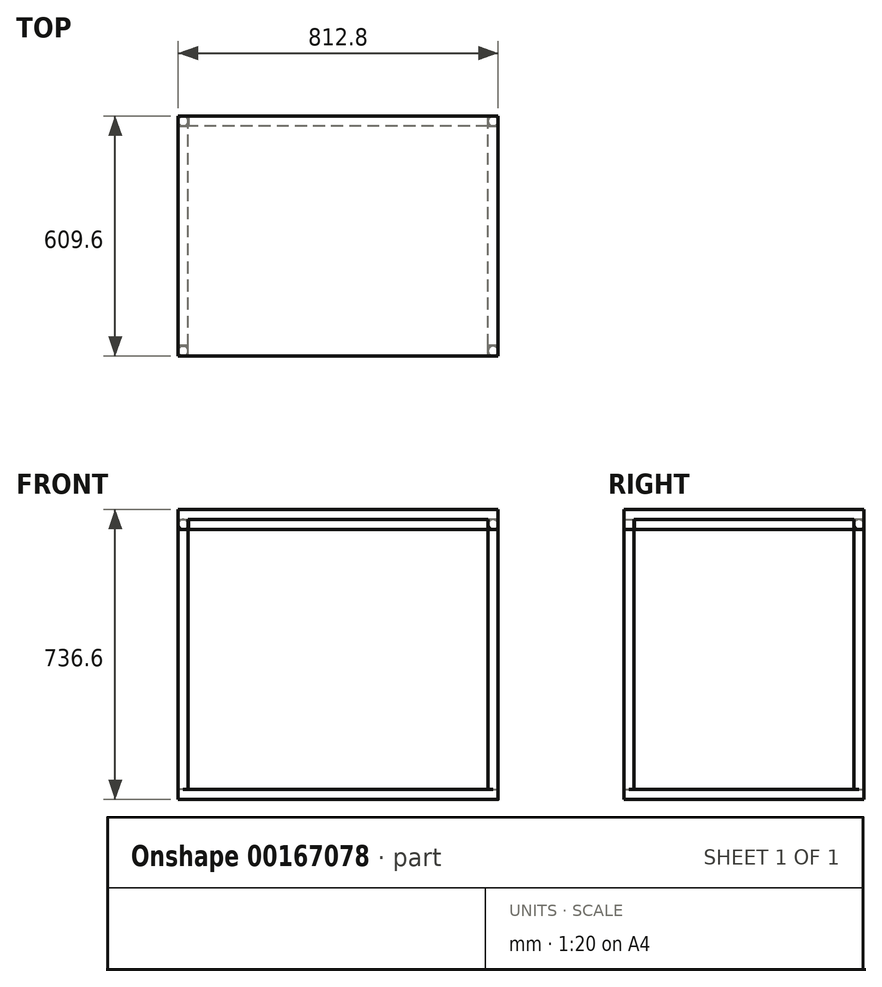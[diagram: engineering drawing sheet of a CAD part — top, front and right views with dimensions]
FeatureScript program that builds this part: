
annotation { "Feature Type Name" : "Feature", "Feature Type Description" : "" }
export const myFeature = defineFeature(function(context is Context, id is Id, definition is map)
    precondition{}
    {
        {
            var Q0;
            Q0=qCreatedBy(makeId("Top.planeOp"),FACE);
            var sketch = newSketch(context, id + "F0", { "sketchPlane" : qUnion([Q0])});
            skLineSegment(sketch, "E0.bottom", {"start": v(406.4, 304.8) * mm, "end": v(-406.4, 304.8) * mm});
            skLineSegment(sketch, "E0.top", {"start": v(406.4, -304.8) * mm, "end": v(-406.4, -304.8) * mm});
            skLineSegment(sketch, "E0.left", {"start": v(406.4, 304.8) * mm, "end": v(406.4, -304.8) * mm});
            skLineSegment(sketch, "E0.right", {"start": v(-406.4, 304.8) * mm, "end": v(-406.4, -304.8) * mm});
            skPoint(sketch, "E0.middle", {"position": v(0, 0) * mm});
            skSolve(sketch);
        }
        {
            var Q0;
            Q0=makeQuery(id+"F0.imprint","IMPRINT",FACE,{"disambiguationData":[TD([[makeQuery(id+"F0.imprint","IMPRINT",EDGE,{"derivedFrom":sQuery(id+"F0.wireOp",EDGE,"E0.bottom")}),1.0]])]});
            extrude(context, id + "F1", {"entities" : qUnion([Q0]), "depth" : 25.4 * mm});
        }
        {
            var Q0;
            Q0=qCreatedBy(makeId("Right.planeOp"),FACE);
            var sketch = newSketch(context, id + "F2", { "sketchPlane" : qUnion([Q0])});
            skLineSegment(sketch, "E1", {"start": v(0, 0) * mm, "end": v(-292.1, 0) * mm});
            skLineSegment(sketch, "E2", {"start": v(0, 0) * mm, "end": v(292.1, 0) * mm});
            skCircle(sketch, "E3", {"center": v(292.1, -12.7) * mm, "radius": 12.7 * mm});
            skSolve(sketch);
        }
        {
            var Q0;
            Q0=qCreatedBy(makeId("Front.planeOp"),FACE);
            var sketch = newSketch(context, id + "F3", { "sketchPlane" : qUnion([Q0])});
            skLineSegment(sketch, "E4", {"start": v(0, 0) * mm, "end": v(-393.7, 0) * mm});
            skLineSegment(sketch, "E5", {"start": v(0, 0) * mm, "end": v(393.7, 0) * mm});
            skCircle(sketch, "E6", {"center": v(-393.7, -12.7) * mm, "radius": 12.7 * mm});
            skCircle(sketch, "E7", {"center": v(393.7, -12.7) * mm, "radius": 12.7 * mm});
            skSolve(sketch);
        }
        {
            var Q0;
            Q0=makeQuery(id+"F1.opExtrude","CAP_FACE",FACE,{"disambiguationData":[OSD([sQuery(id+"F0.wireOp",EDGE,"E0.bottom"),sQuery(id+"F0.wireOp",EDGE,"E0.top"),sQuery(id+"F0.wireOp",EDGE,"E0.left"),sQuery(id+"F0.wireOp",EDGE,"E0.right")])],"isStart":true});
            var sketch = newSketch(context, id + "F4", { "sketchPlane" : qUnion([Q0])});
            skPoint(sketch, "E8.middle", {"position": v(-406.4, -304.8) * mm});
            skLineSegment(sketch, "E9.bottom", {"start": v(-406.4, -304.8) * mm, "end": v(-381, -304.8) * mm});
            skLineSegment(sketch, "E9.top", {"start": v(-406.4, -279.4) * mm, "end": v(-381, -279.4) * mm});
            skLineSegment(sketch, "E9.left", {"start": v(-406.4, -304.8) * mm, "end": v(-406.4, -279.4) * mm});
            skLineSegment(sketch, "E9.right", {"start": v(-381, -304.8) * mm, "end": v(-381, -279.4) * mm});
            skLineSegment(sketch, "E10.bottom", {"start": v(406.4, -304.8) * mm, "end": v(381, -304.8) * mm});
            skLineSegment(sketch, "E10.top", {"start": v(406.4, -279.4) * mm, "end": v(381, -279.4) * mm});
            skLineSegment(sketch, "E10.left", {"start": v(406.4, -304.8) * mm, "end": v(406.4, -279.4) * mm});
            skLineSegment(sketch, "E10.right", {"start": v(381, -304.8) * mm, "end": v(381, -279.4) * mm});
            skLineSegment(sketch, "E11.bottom", {"start": v(406.4, 304.8) * mm, "end": v(381, 304.8) * mm});
            skLineSegment(sketch, "E11.top", {"start": v(406.4, 279.4) * mm, "end": v(381, 279.4) * mm});
            skLineSegment(sketch, "E11.left", {"start": v(406.4, 304.8) * mm, "end": v(406.4, 279.4) * mm});
            skLineSegment(sketch, "E11.right", {"start": v(381, 304.8) * mm, "end": v(381, 279.4) * mm});
            skLineSegment(sketch, "E12.bottom", {"start": v(-406.4, 304.8) * mm, "end": v(-381, 304.8) * mm});
            skLineSegment(sketch, "E12.top", {"start": v(-406.4, 279.4) * mm, "end": v(-381, 279.4) * mm});
            skLineSegment(sketch, "E12.left", {"start": v(-406.4, 304.8) * mm, "end": v(-406.4, 279.4) * mm});
            skLineSegment(sketch, "E12.right", {"start": v(-381, 304.8) * mm, "end": v(-381, 279.4) * mm});
            skSolve(sketch);
        }
        {
            var Q0;
            Q0 = qSketchRegion(id + "F4", true);
            extrude(context, id + "F5", {"entities" : qUnion([Q0]), "operationType" : NewBodyOperationType.ADD, "depth" : 25.4 * mm});
        }
        {
            var Q0;
            Q0=qCreatedBy(makeId("Top.planeOp"),FACE);
            cPlane(context, id + "F6", {"entities" : qUnion([Q0]), "cplaneType" : CPlaneType.OFFSET, "offset" : 25.4 * mm, "oppositeDirection" : true, "width" : 152.4 * mm, "height" : 152.4 * mm});
        }
        {
            var Q0;
            Q0=qCreatedBy(id+"F6.planeOp",FACE);
            var sketch = newSketch(context, id + "F7", { "sketchPlane" : qUnion([Q0])});
            skLineSegment(sketch, "E13", {"start": v(0, 0) * mm, "end": v(-393.7, 0) * mm});
            skLineSegment(sketch, "E14", {"start": v(-393.7, 0) * mm, "end": v(-393.7, -292.1) * mm});
            skLineSegment(sketch, "E15", {"start": v(0, 0) * mm, "end": v(393.7, 0) * mm});
            skLineSegment(sketch, "E16", {"start": v(393.7, 0) * mm, "end": v(393.7, 292.1) * mm});
            skCircle(sketch, "E17", {"center": v(-393.7, -292.1) * mm, "radius": 12.7 * mm});
            skCircle(sketch, "E18", {"center": v(-393.7, 292.1) * mm, "radius": 12.7 * mm});
            skCircle(sketch, "E19", {"center": v(393.7, 292.1) * mm, "radius": 12.7 * mm});
            skCircle(sketch, "E20", {"center": v(393.7, -292.1) * mm, "radius": 12.7 * mm});
            skSolve(sketch);
        }
        {
            var Q0;
            Q0 = qSketchRegion(id + "F7", true);
            extrude(context, id + "F8", {"entities" : qUnion([Q0]), "operationType" : NewBodyOperationType.ADD, "oppositeDirection" : true, "depth" : 685.8 * mm});
        }
        {
            var Q0;
            Q0=qCreatedBy(makeId("Top.planeOp"),FACE);
            cPlane(context, id + "F9", {"entities" : qUnion([Q0]), "cplaneType" : CPlaneType.OFFSET, "offset" : 711.2 * mm, "oppositeDirection" : true, "width" : 152.4 * mm, "height" : 152.4 * mm});
        }
        {
            var Q0;
            Q0=qCreatedBy(id+"F9.planeOp",FACE);
            var sketch = newSketch(context, id + "F10", { "sketchPlane" : qUnion([Q0])});
            skLineSegment(sketch, "E21.bottom", {"start": v(406.4, -304.8) * mm, "end": v(-406.4, -304.8) * mm});
            skLineSegment(sketch, "E21.top", {"start": v(406.4, 304.8) * mm, "end": v(-406.4, 304.8) * mm});
            skLineSegment(sketch, "E21.left", {"start": v(406.4, -304.8) * mm, "end": v(406.4, 304.8) * mm});
            skLineSegment(sketch, "E21.right", {"start": v(-406.4, -304.8) * mm, "end": v(-406.4, 304.8) * mm});
            skPoint(sketch, "E21.middle", {"position": v(0, 0) * mm});
            skSolve(sketch);
        }
        {
            var Q0;
            Q0=makeQuery(id+"F10.imprint","IMPRINT",FACE,{"disambiguationData":[TD([[makeQuery(id+"F10.imprint","IMPRINT",EDGE,{"derivedFrom":sQuery(id+"F10.wireOp",EDGE,"E21.bottom")}),-1.0]])]});
            extrude(context, id + "F11", {"entities" : qUnion([Q0]), "operationType" : NewBodyOperationType.ADD, "depth" : 25.4 * mm});
        }
        {
            var Q0;
            Q0=makeQuery(id+"F11.opExtrude","SWEPT_EDGE",EDGE,{"disambiguationData":[OSD([sQuery(id+"F10.wireOp",EDGE,"E21.top"),sQuery(id+"F10.wireOp",EDGE,"E21.right")])]});
            var Q1;
            Q1=makeQuery(id+"F11.opExtrude","SWEPT_EDGE",EDGE,{"disambiguationData":[OSD([sQuery(id+"F10.wireOp",EDGE,"E21.bottom"),sQuery(id+"F10.wireOp",EDGE,"E21.right")])]});
            var Q2;
            Q2=makeQuery(id+"F11.opExtrude","SWEPT_EDGE",EDGE,{"disambiguationData":[OSD([sQuery(id+"F10.wireOp",EDGE,"E21.bottom"),sQuery(id+"F10.wireOp",EDGE,"E21.left")])]});
            var Q3;
            Q3=makeQuery(id+"F11.opExtrude","SWEPT_EDGE",EDGE,{"disambiguationData":[OSD([sQuery(id+"F10.wireOp",EDGE,"E21.top"),sQuery(id+"F10.wireOp",EDGE,"E21.left")])]});
            fillet(context, id + "F12", {"entities" : qUnion([Q0, Q1, Q2, Q3]), "radius" : 12.7 * mm, "tangentPropagation" : true, "allowEdgeOverflow" : false});
        }
        {
            var Q0;
            Q0=makeQuery(id+"F3.imprint","IMPRINT",FACE,{"disambiguationData":[TD([[makeQuery(id+"F3.imprint","IMPRINT",EDGE,{"derivedFrom":sQuery(id+"F3.wireOp",EDGE,"E7")}),1.0]])]});
            var Q1;
            Q1=makeQuery(id+"F3.imprint","IMPRINT",FACE,{"disambiguationData":[TD([[makeQuery(id+"F3.imprint","IMPRINT",EDGE,{"derivedFrom":sQuery(id+"F3.wireOp",EDGE,"E6")}),1.0]])]});
            extrude(context, id + "F13", {"entities" : qUnion([Q0, Q1]), "operationType" : NewBodyOperationType.ADD, "endBound" : BoundingType.SYMMETRIC, "depth" : 557.53 * mm});
        }
        {
            var Q0;
            Q0=makeQuery(id+"F2.imprint","IMPRINT",FACE,{"disambiguationData":[TD([[makeQuery(id+"F2.imprint","IMPRINT",EDGE,{"derivedFrom":sQuery(id+"F2.wireOp",EDGE,"GIRA73NO-ARli-Yjb9-NUIK-CAwgFWsL4eDN")}),1.0]])]});
            var Q1;
            Q1=makeQuery(id+"F2.imprint","IMPRINT",FACE,{"disambiguationData":[TD([[makeQuery(id+"F2.imprint","IMPRINT",EDGE,{"derivedFrom":sQuery(id+"F2.wireOp",EDGE,"E3")}),1.0]])]});
            extrude(context, id + "F14", {"entities" : qUnion([Q0, Q1]), "operationType" : NewBodyOperationType.ADD, "endBound" : BoundingType.SYMMETRIC, "depth" : 760.73 * mm});
        }
    });
